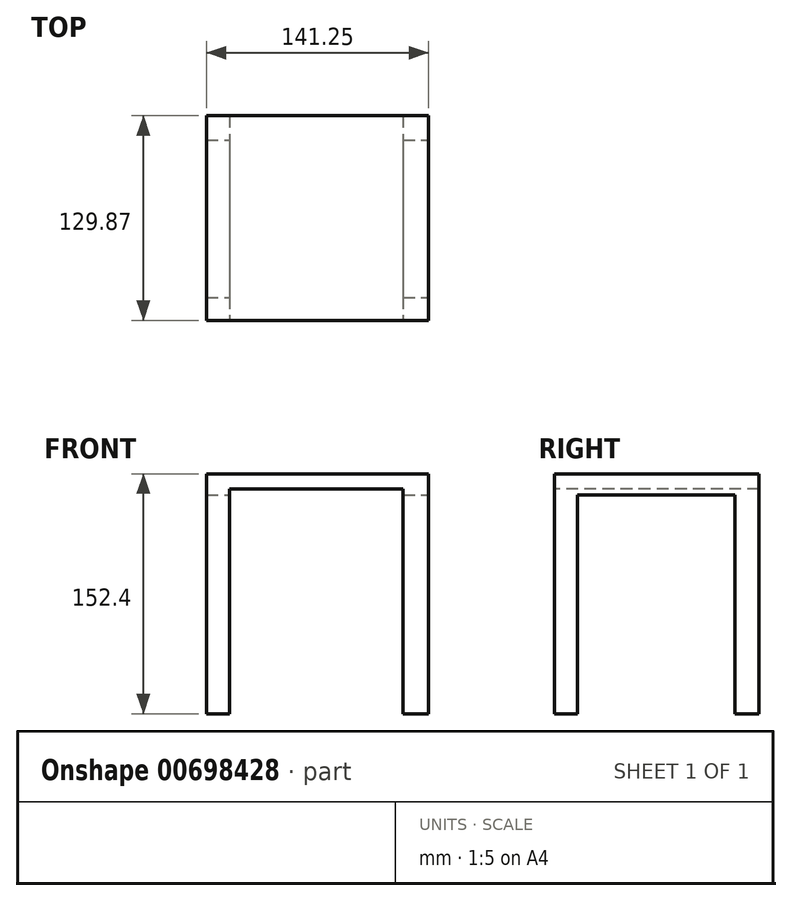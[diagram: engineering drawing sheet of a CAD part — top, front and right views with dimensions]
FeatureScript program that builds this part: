
annotation { "Feature Type Name" : "Feature", "Feature Type Description" : "" }
export const myFeature = defineFeature(function(context is Context, id is Id, definition is map)
    precondition{}
    {
        {
            var Q0;
            Q0=qCreatedBy(makeId("Top.planeOp"),FACE);
            var sketch = newSketch(context, id + "F0", { "sketchPlane" : qUnion([Q0])});
            skLineSegment(sketch, "E0.bottom", {"start": v(-124.94, 64.72) * mm, "end": v(16.31, 64.72) * mm});
            skLineSegment(sketch, "E0.top", {"start": v(-124.94, -65.15) * mm, "end": v(16.31, -65.15) * mm});
            skLineSegment(sketch, "E0.left", {"start": v(-124.94, 64.72) * mm, "end": v(-124.94, -65.15) * mm});
            skLineSegment(sketch, "E0.right", {"start": v(16.31, 64.72) * mm, "end": v(16.31, -65.15) * mm});
            skSolve(sketch);
        }
        {
            var Q0;
            Q0 = qSketchRegion(id + "F0", true);
            extrude(context, id + "F1", {"entities" : qUnion([Q0]), "depth" : 152.4 * mm, "offsetDistance" : 25.4 * mm});
        }
        {
            var Q0;
            Q0=makeQuery(id+"F1.opExtrude","SWEPT_FACE",FACE,{"disambiguationData":[OSD([sQuery(id+"F0.wireOp",EDGE,"E0.top")])]});
            var sketch = newSketch(context, id + "F2", { "sketchPlane" : qUnion([Q0])});
            skLineSegment(sketch, "E1.bottom", {"start": v(-110.18, 142.78) * mm, "end": v(0, 142.78) * mm});
            skLineSegment(sketch, "E1.top", {"start": v(-110.18, 0) * mm, "end": v(0, 0) * mm});
            skLineSegment(sketch, "E1.left", {"start": v(-110.18, 142.78) * mm, "end": v(-110.18, 0) * mm});
            skLineSegment(sketch, "E1.right", {"start": v(0, 142.78) * mm, "end": v(0, 0) * mm});
            skSolve(sketch);
        }
        {
            var Q0;
            Q0 = qSketchRegion(id + "F2", true);
            extrude(context, id + "F3", {"entities" : qUnion([Q0]), "operationType" : NewBodyOperationType.REMOVE, "oppositeDirection" : true, "depth" : 152.4 * mm, "offsetDistance" : 25.4 * mm});
        }
        {
            var Q0;
            Q0=makeQuery(id+"F1.opExtrude","SWEPT_FACE",FACE,{"disambiguationData":[OSD([sQuery(id+"F0.wireOp",EDGE,"E0.right")])]});
            var sketch = newSketch(context, id + "F4", { "sketchPlane" : qUnion([Q0])});
            skLineSegment(sketch, "E2.bottom", {"start": v(-50.62, 138.8) * mm, "end": v(49.42, 138.8) * mm});
            skLineSegment(sketch, "E2.top", {"start": v(-50.62, -0.16) * mm, "end": v(49.42, -0.16) * mm});
            skLineSegment(sketch, "E2.left", {"start": v(-50.62, 138.8) * mm, "end": v(-50.62, -0.16) * mm});
            skLineSegment(sketch, "E2.right", {"start": v(49.42, 138.8) * mm, "end": v(49.42, -0.16) * mm});
            skSolve(sketch);
        }
        {
            var Q0;
            {var subQ0=sQuery(id+"F4.wireOp",EDGE,"E2.bottom");Q0=makeQuery(id+"F4.imprint","IMPRINT",FACE,{"disambiguationData":[TD([[makeQuery(id+"F4.imprint","IMPRINT",EDGE,{"derivedFrom":subQ0}),-1.0]])]});}
            extrude(context, id + "F5", {"entities" : qUnion([Q0]), "operationType" : NewBodyOperationType.REMOVE, "oppositeDirection" : true, "depth" : 152.4 * mm, "offsetDistance" : 25.4 * mm});
        }
    });
